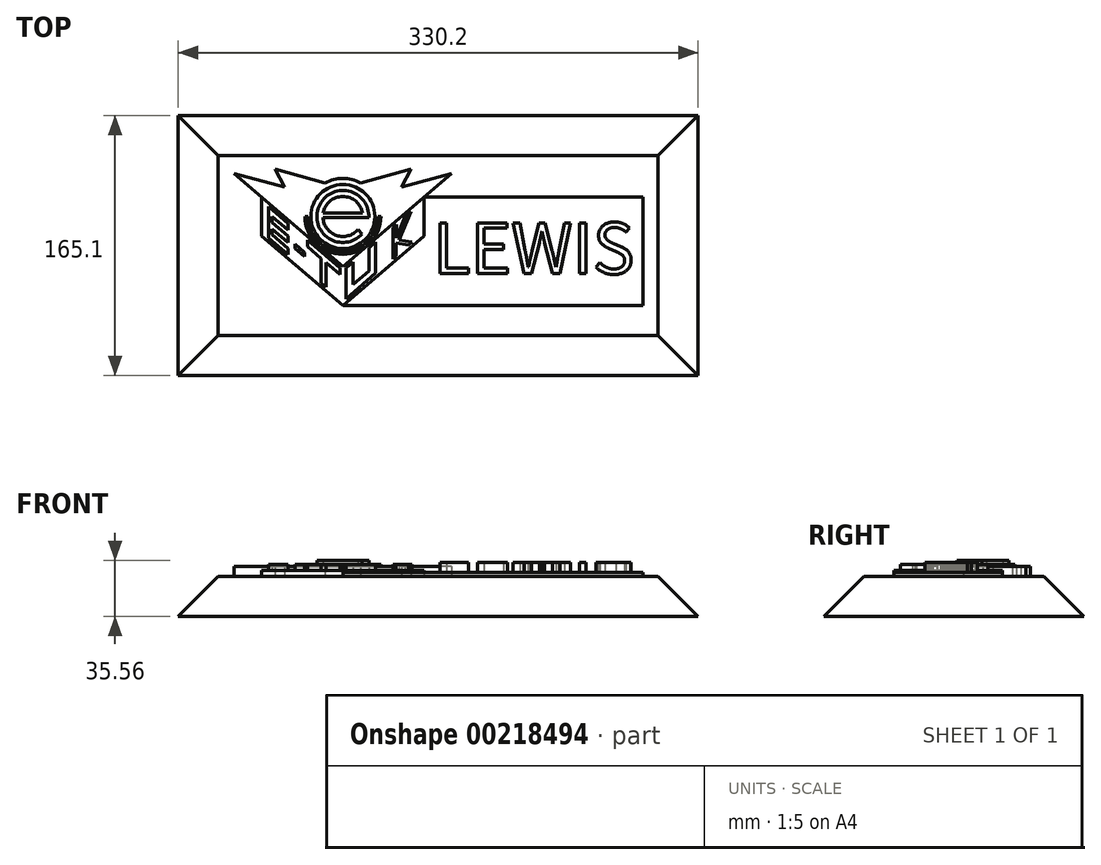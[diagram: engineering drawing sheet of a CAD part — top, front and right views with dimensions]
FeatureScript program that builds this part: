
annotation { "Feature Type Name" : "Feature", "Feature Type Description" : "" }
export const myFeature = defineFeature(function(context is Context, id is Id, definition is map)
    precondition{}
    {
        {
            var Q0;
            Q0=qCreatedBy(makeId("Top.planeOp"),FACE);
            var sketch = newSketch(context, id + "F0", { "sketchPlane" : qUnion([Q0])});
            skArc(sketch, "E0", {"start": v(12.53, 2.07) * mm, "mid": v(0, 12.7) * mm, "end": v(-12.53, 2.07) * mm});
            skArc(sketch, "E1", {"start": v(16.5, -0.78) * mm, "mid": v(-15.23, 6.37) * mm, "end": v(12.14, -11.18) * mm});
            skLineSegment(sketch, "E2", {"start": v(12.7, -0.78) * mm, "end": v(-12.68, -0.78) * mm});
            skLineSegment(sketch, "E3", {"start": v(-12.68, -0.78) * mm, "end": v(16.5, -0.78) * mm});
            skLineSegment(sketch, "E4", {"start": v(9.59, -8.33) * mm, "end": v(12.14, -11.18) * mm});
            skArc(sketch, "E5.trimOffspring", {"start": v(-12.68, -0.78) * mm, "mid": v(-4.08, -12.03) * mm, "end": v(9.59, -8.33) * mm});
            skLineSegment(sketch, "E6", {"start": v(-12.53, 2.07) * mm, "end": v(12.53, 2.07) * mm});
            skSolve(sketch);
        }
        {
            var Q0;
            Q0=makeQuery(id+"F0.imprint","IMPRINT",FACE,{"disambiguationData":[TD([[makeQuery(id+"F0.imprint","IMPRINT",EDGE,{"derivedFrom":sQuery(id+"F0.wireOp",EDGE,"E0")}),-1.0]])]});
            extrude(context, id + "F1", {"entities" : qUnion([Q0]), "depth" : 10.16 * mm});
        }
        {
            var Q0;
            Q0=qCreatedBy(makeId("Top.planeOp"),FACE);
            var sketch = newSketch(context, id + "F2", { "sketchPlane" : qUnion([Q0])});
            skCircle(sketch, "E7", {"center": v(0, 0) * mm, "radius": 20.32 * mm});
            skSolve(sketch);
        }
        {
            var Q0;
            Q0=qSketchRegion(id+"F2",true);
            extrude(context, id + "F3", {"entities" : qUnion([Q0]), "operationType" : NewBodyOperationType.ADD, "depth" : 7.62 * mm});
        }
        {
            var Q0;
            Q0=qCreatedBy(makeId("Top.planeOp"),FACE);
            var sketch = newSketch(context, id + "F4", { "sketchPlane" : qUnion([Q0])});
            skLineSegment(sketch, "E8", {"start": v(-69.02, 27.27) * mm, "end": v(-37.13, 18.72) * mm});
            skLineSegment(sketch, "E9", {"start": v(-37.13, 18.72) * mm, "end": v(-43.14, 30.14) * mm});
            skLineSegment(sketch, "E10", {"start": v(-43.14, 30.14) * mm, "end": v(-11.32, 21.31) * mm});
            skLineSegment(sketch, "E11", {"start": v(-69.02, 27.27) * mm, "end": v(0, -31.75) * mm});
            skLineSegment(sketch, "E12.MirrorCS", {"start": v(43.14, 30.14) * mm, "end": v(11.32, 21.31) * mm});
            skLineSegment(sketch, "E13.MirrorCS", {"start": v(69.02, 27.27) * mm, "end": v(0, -31.75) * mm});
            skLineSegment(sketch, "E14.MirrorCS", {"start": v(69.02, 27.27) * mm, "end": v(37.13, 18.72) * mm});
            skLineSegment(sketch, "E15.MirrorCS", {"start": v(37.13, 18.72) * mm, "end": v(43.14, 30.14) * mm});
            skArc(sketch, "E16.trimOffspring", {"start": v(11.32, 21.31) * mm, "mid": v(0, 24.13) * mm, "end": v(-11.32, 21.31) * mm});
            skSolve(sketch);
        }
        {
            var Q0;
            Q0=qSketchRegion(id+"F4",true);
            var Q1;
            Q1=makeQuery(id+"F2.imprint","IMPRINT",FACE,{"disambiguationData":[TD([[makeQuery(id+"F2.imprint","IMPRINT",EDGE,{"derivedFrom":sQuery(id+"F2.wireOp",EDGE,"E7")}),1.0]])]});
            extrude(context, id + "F5", {"entities" : qUnion([Q0, Q1]), "operationType" : NewBodyOperationType.ADD, "depth" : 6.35 * mm});
        }
        {
            var Q0;
            Q0=qCreatedBy(makeId("Top.planeOp"),FACE);
            var sketch = newSketch(context, id + "F6", { "sketchPlane" : qUnion([Q0])});
            skLineSegment(sketch, "E17", {"start": v(-51.6, -12.38) * mm, "end": v(0, -56.51) * mm});
            skLineSegment(sketch, "E18", {"start": v(0, -56.51) * mm, "end": v(51.6, -12.38) * mm});
            skLineSegment(sketch, "E19", {"start": v(-51.6, 12.38) * mm, "end": v(-51.6, -12.38) * mm});
            skLineSegment(sketch, "E20", {"start": v(51.6, 12.38) * mm, "end": v(51.6, -12.38) * mm});
            skLineSegment(sketch, "E21", {"start": v(-51.6, 12.38) * mm, "end": v(0, -31.75) * mm});
            skLineSegment(sketch, "E22", {"start": v(0, -31.75) * mm, "end": v(51.6, 12.38) * mm});
            skSolve(sketch);
        }
        {
            var Q0;
            Q0=qSketchRegion(id+"F6",true);
            extrude(context, id + "F7", {"entities" : qUnion([Q0]), "operationType" : NewBodyOperationType.ADD, "depth" : 3.8 * mm});
        }
        {
            var Q0;
            Q0=makeQuery(id+"F7.opExtrude","CAP_FACE",FACE,{"disambiguationData":[OSD([sQuery(id+"F6.wireOp",EDGE,"E17"),sQuery(id+"F6.wireOp",EDGE,"E18"),sQuery(id+"F6.wireOp",EDGE,"E19"),sQuery(id+"F6.wireOp",EDGE,"E20"),sQuery(id+"F6.wireOp",EDGE,"E21"),sQuery(id+"F6.wireOp",EDGE,"E22")])],"isStart":false});
            var sketch = newSketch(context, id + "F8", { "sketchPlane" : qUnion([Q0])});
            skPoint(sketch, "E23.startSnap0", {"position": v(-51.6, 0) * mm});
            skLineSegment(sketch, "E24", {"start": v(-51.6, -9.87) * mm, "end": v(-51.6, 9.87) * mm, "construction": true});
            skLineSegment(sketch, "E25", {"start": v(-47.26, 6.16) * mm, "end": v(-34.74, -4.55) * mm});
            skLineSegment(sketch, "E26", {"start": v(-34.74, -4.55) * mm, "end": v(-34.74, -8.63) * mm});
            skLineSegment(sketch, "E27", {"start": v(-34.74, -8.63) * mm, "end": v(-44.83, 0) * mm});
            skLineSegment(sketch, "E28", {"start": v(-44.83, 0) * mm, "end": v(-44.83, -3.75) * mm});
            skLineSegment(sketch, "E29", {"start": v(-44.83, -3.75) * mm, "end": v(-34.74, -12.38) * mm});
            skLineSegment(sketch, "E30", {"start": v(-34.74, -12.38) * mm, "end": v(-34.74, -16.46) * mm});
            skLineSegment(sketch, "E31", {"start": v(-34.74, -16.46) * mm, "end": v(-44.83, -7.83) * mm});
            skLineSegment(sketch, "E32", {"start": v(-44.83, -7.83) * mm, "end": v(-44.83, -11.58) * mm});
            skLineSegment(sketch, "E33", {"start": v(-44.83, -11.58) * mm, "end": v(-34.74, -20.21) * mm});
            skLineSegment(sketch, "E34", {"start": v(-34.74, -20.21) * mm, "end": v(-34.74, -24.3) * mm});
            skLineSegment(sketch, "E35", {"start": v(-34.74, -24.3) * mm, "end": v(-47.26, -13.59) * mm});
            skLineSegment(sketch, "E36", {"start": v(-47.26, 6.16) * mm, "end": v(-47.26, -13.59) * mm});
            skLineSegment(sketch, "E37", {"start": v(-30.38, -20.21) * mm, "end": v(-30.38, -17.65) * mm});
            skLineSegment(sketch, "E38", {"start": v(-30.38, -17.65) * mm, "end": v(-24.17, -22.96) * mm});
            skLineSegment(sketch, "E39", {"start": v(-24.17, -22.96) * mm, "end": v(-24.17, -25.53) * mm});
            skLineSegment(sketch, "E40", {"start": v(-24.17, -25.53) * mm, "end": v(-30.38, -20.21) * mm});
            skLineSegment(sketch, "E41", {"start": v(-22.38, -15.12) * mm, "end": v(-1.9, -32.63) * mm});
            skLineSegment(sketch, "E42", {"start": v(-1.9, -32.63) * mm, "end": v(-1.9, -36.71) * mm});
            skLineSegment(sketch, "E43", {"start": v(-1.9, -36.71) * mm, "end": v(-10.6, -29.28) * mm});
            skLineSegment(sketch, "E44", {"start": v(-10.6, -29.28) * mm, "end": v(-10.6, -44.95) * mm});
            skLineSegment(sketch, "E45", {"start": v(-10.6, -44.95) * mm, "end": v(-13.7, -42.3) * mm});
            skLineSegment(sketch, "E46", {"start": v(-13.7, -42.3) * mm, "end": v(-13.7, -26.63) * mm});
            skLineSegment(sketch, "E47", {"start": v(-13.7, -26.63) * mm, "end": v(-22.38, -19.2) * mm});
            skLineSegment(sketch, "E48", {"start": v(-22.38, -19.2) * mm, "end": v(-22.38, -15.12) * mm});
            skLineSegment(sketch, "E49", {"start": v(1.9, -32.62) * mm, "end": v(6.3, -28.86) * mm});
            skLineSegment(sketch, "E50", {"start": v(6.3, -28.86) * mm, "end": v(6.3, -43.26) * mm});
            skLineSegment(sketch, "E51", {"start": v(6.3, -43.26) * mm, "end": v(16.5, -34.54) * mm});
            skLineSegment(sketch, "E52", {"start": v(16.5, -34.54) * mm, "end": v(16.5, -20.14) * mm});
            skLineSegment(sketch, "E53", {"start": v(16.5, -20.14) * mm, "end": v(20.85, -16.3) * mm});
            skLineSegment(sketch, "E54", {"start": v(20.85, -16.3) * mm, "end": v(20.85, -36.06) * mm});
            skLineSegment(sketch, "E55", {"start": v(20.85, -36.06) * mm, "end": v(1.9, -52.37) * mm});
            skLineSegment(sketch, "E56", {"start": v(1.9, -52.37) * mm, "end": v(1.9, -32.62) * mm});
            skLineSegment(sketch, "E57", {"start": v(31.73, -7.12) * mm, "end": v(31.73, -27.15) * mm});
            skLineSegment(sketch, "E58", {"start": v(31.73, -27.15) * mm, "end": v(33.91, -25.22) * mm});
            skLineSegment(sketch, "E59", {"start": v(33.91, -25.22) * mm, "end": v(33.91, -16.82) * mm});
            skLineSegment(sketch, "E60", {"start": v(33.94, -13.64) * mm, "end": v(33.94, -5.23) * mm});
            skLineSegment(sketch, "E61", {"start": v(33.94, -5.23) * mm, "end": v(31.73, -7.12) * mm});
            skLineSegment(sketch, "E62", {"start": v(41.79, -18.27) * mm, "end": v(44, -16.38) * mm});
            skLineSegment(sketch, "E63", {"start": v(33.94, -13.64) * mm, "end": v(39.5, 0) * mm});
            skLineSegment(sketch, "E64", {"start": v(33.91, -16.82) * mm, "end": v(41.79, -18.27) * mm});
            skLineSegment(sketch, "E65", {"start": v(44, -16.38) * mm, "end": v(35.85, -14.87) * mm});
            skLineSegment(sketch, "E66", {"start": v(35.85, -14.87) * mm, "end": v(43.2, 3.16) * mm});
            skLineSegment(sketch, "E67", {"start": v(39.5, 0) * mm, "end": v(43.2, 3.16) * mm});
            skSolve(sketch);
        }
        {
            var Q0;
            Q0=qSketchRegion(id+"F8",true);
            extrude(context, id + "F9", {"entities" : qUnion([Q0]), "operationType" : NewBodyOperationType.ADD, "depth" : 3.8 * mm});
        }
        {
            var Q0;
            Q0=makeQuery(id+"F5.boolean.opBoolean","MERGE",FACE,{"derivedFrom":[makeQuery(id+"F5.opExtrude","CAP_FACE",FACE,{"disambiguationData":[OSD([sQuery(id+"F2.wireOp",EDGE,"E7")])],"isStart":false}),makeQuery(id+"F5.opExtrude","CAP_FACE",FACE,{"disambiguationData":[OSD([sQuery(id+"F4.wireOp",EDGE,"E8"),sQuery(id+"F4.wireOp",EDGE,"E9"),sQuery(id+"F4.wireOp",EDGE,"E10"),sQuery(id+"F4.wireOp",EDGE,"E11"),sQuery(id+"F4.wireOp",EDGE,"E13.MirrorCS"),sQuery(id+"F4.wireOp",EDGE,"E14.MirrorCS"),sQuery(id+"F4.wireOp",EDGE,"E12.MirrorCS"),sQuery(id+"F4.wireOp",EDGE,"E15.MirrorCS"),sQuery(id+"F4.wireOp",EDGE,"E16.trimOffspring")])],"isStart":false})]});
            var sketch = newSketch(context, id + "F10", { "sketchPlane" : qUnion([Q0])});
            skArc(sketch, "E68", {"start": v(-24.13, 0) * mm, "mid": v(0, -24.13) * mm, "end": v(24.13, 0) * mm});
            skArc(sketch, "E69", {"start": v(-22.23, 0) * mm, "mid": v(0, -22.23) * mm, "end": v(22.23, 0) * mm});
            skLineSegment(sketch, "E70", {"start": v(-24.13, 0) * mm, "end": v(-22.23, 0) * mm});
            skLineSegment(sketch, "E71", {"start": v(24.13, 0) * mm, "end": v(22.23, 0) * mm});
            skSolve(sketch);
        }
        {
            var Q0;
            Q0=qSketchRegion(id+"F10",true);
            extrude(context, id + "F11", {"entities" : qUnion([Q0]), "operationType" : NewBodyOperationType.ADD, "depth" : 1.27 * mm});
        }
        {
            var Q0;
            {var subQ0=sQuery(id+"F2.wireOp",EDGE,"E7");Q0=makeQuery(id+"F7.boolean.opBoolean","MERGE",FACE,{"derivedFrom":[makeQuery(id+"F5.boolean.opBoolean","MERGE",FACE,{"derivedFrom":[makeQuery(id+"F3.boolean.opBoolean","MERGE",FACE,{"derivedFrom":[makeQuery(id+"F1.opExtrude","CAP_FACE",FACE,{"disambiguationData":[OSD([sQuery(id+"F0.wireOp",EDGE,"E0"),sQuery(id+"F0.wireOp",EDGE,"E1"),sQuery(id+"F0.wireOp",EDGE,"E3"),sQuery(id+"F0.wireOp",EDGE,"E4"),sQuery(id+"F0.wireOp",EDGE,"E5.trimOffspring"),sQuery(id+"F0.wireOp",EDGE,"E6")])],"isStart":true}),makeQuery(id+"F3.opExtrude","CAP_FACE",FACE,{"disambiguationData":[OSD([subQ0])],"isStart":true})]}),makeQuery(id+"F5.opExtrude","CAP_FACE",FACE,{"disambiguationData":[OSD([subQ0])],"isStart":true}),makeQuery(id+"F5.opExtrude","CAP_FACE",FACE,{"disambiguationData":[OSD([sQuery(id+"F4.wireOp",EDGE,"E8"),sQuery(id+"F4.wireOp",EDGE,"E9"),sQuery(id+"F4.wireOp",EDGE,"E10"),sQuery(id+"F4.wireOp",EDGE,"E11"),sQuery(id+"F4.wireOp",EDGE,"E13.MirrorCS"),sQuery(id+"F4.wireOp",EDGE,"E14.MirrorCS"),sQuery(id+"F4.wireOp",EDGE,"E12.MirrorCS"),sQuery(id+"F4.wireOp",EDGE,"E15.MirrorCS"),sQuery(id+"F4.wireOp",EDGE,"E16.trimOffspring")])],"isStart":true})]}),makeQuery(id+"F7.opExtrude","CAP_FACE",FACE,{"disambiguationData":[OSD([sQuery(id+"F6.wireOp",EDGE,"E17"),sQuery(id+"F6.wireOp",EDGE,"E18"),sQuery(id+"F6.wireOp",EDGE,"E19"),sQuery(id+"F6.wireOp",EDGE,"E20"),sQuery(id+"F6.wireOp",EDGE,"E21"),sQuery(id+"F6.wireOp",EDGE,"E22")])],"isStart":true})]});}
            var sketch = newSketch(context, id + "F12", { "sketchPlane" : qUnion([Q0])});
            skLineSegment(sketch, "E72.bottom", {"start": v(0, 56.51) * mm, "end": v(190.5, 56.51) * mm});
            skLineSegment(sketch, "E72.right", {"start": v(190.5, 56.51) * mm, "end": v(190.5, -12.38) * mm});
            skLineSegment(sketch, "E73", {"start": v(51.6, -12.38) * mm, "end": v(190.5, -12.38) * mm});
            skLineSegment(sketch, "E74", {"start": v(0, 56.51) * mm, "end": v(51.6, 12.38) * mm});
            skLineSegment(sketch, "E75", {"start": v(51.6, 12.38) * mm, "end": v(51.6, -12.38) * mm});
            skSolve(sketch);
        }
        {
            var Q0;
            Q0=qSketchRegion(id+"F12",true);
            extrude(context, id + "F13", {"entities" : qUnion([Q0]), "operationType" : NewBodyOperationType.ADD, "oppositeDirection" : true, "depth" : 2.54 * mm});
        }
        {
            var Q0;
            Q0=makeQuery(id+"F13.opExtrude","CAP_FACE",FACE,{"disambiguationData":[OSD([sQuery(id+"F12.wireOp",EDGE,"E72.bottom"),sQuery(id+"F12.wireOp",EDGE,"E72.right"),sQuery(id+"F12.wireOp",EDGE,"E73"),sQuery(id+"F12.wireOp",EDGE,"E74"),sQuery(id+"F12.wireOp",EDGE,"E75")])],"isStart":false});
            var sketch = newSketch(context, id + "F14", { "sketchPlane" : qUnion([Q0])});
            skLineSegment(sketch, "E76", {"start": v(51.6, 12.38) * mm, "end": v(51.6, -56.51) * mm, "construction": true});
            skLineSegment(sketch, "E77", {"start": v(51.6, -56.51) * mm, "end": v(190.5, -56.51) * mm, "construction": true});
            skLineSegment(sketch, "E78", {"start": v(190.5, -56.51) * mm, "end": v(190.5, 12.38) * mm, "construction": true});
            skLineSegment(sketch, "E79", {"start": v(190.5, 12.38) * mm, "end": v(51.6, 12.38) * mm, "construction": true});
            skPoint(sketch, "E80.startSnap0", {"position": v(51.6, 0) * mm});
            skPoint(sketch, "E80.endSnap0", {"position": v(51.6, 0) * mm});
            skLineSegment(sketch, "E81", {"start": v(185.58, -36.36) * mm, "end": v(57.26, -36.36) * mm, "construction": true});
            skLineSegment(sketch, "E82", {"start": v(178.12, -4.6) * mm, "end": v(57.26, -4.6) * mm, "construction": true});
            skText(sketch, "E83", { "text": "LEWIS", "fontName": "NotoSansCJKkr-Regular.otf"});
            const initialGuessF14  = {"E83": [0.05726, -0.03636, 1, 0, 0.03175]};
            skSetInitialGuess(sketch, initialGuessF14);
            skSolve(sketch);
        }
        {
            var Q0;
            Q0=qSketchRegion(id+"F14",true);
            extrude(context, id + "F15", {"entities" : qUnion([Q0]), "operationType" : NewBodyOperationType.ADD, "depth" : 6.35 * mm});
        }
        {
            var Q0;
            Q0=makeQuery(id+"F13.opExtrude","CAP_FACE",FACE,{"disambiguationData":[OSD([sQuery(id+"F12.wireOp",EDGE,"E72.bottom"),sQuery(id+"F12.wireOp",EDGE,"E72.right"),sQuery(id+"F12.wireOp",EDGE,"E73"),sQuery(id+"F12.wireOp",EDGE,"E74"),sQuery(id+"F12.wireOp",EDGE,"E75")])],"isStart":true});
            var sketch = newSketch(context, id + "F16", { "sketchPlane" : qUnion([Q0])});
            skLineSegment(sketch, "E84.bottom", {"start": v(-79.18, -38.74) * mm, "end": v(200.22, -38.74) * mm});
            skLineSegment(sketch, "E84.top", {"start": v(-79.18, 75.56) * mm, "end": v(200.22, 75.56) * mm});
            skLineSegment(sketch, "E84.left", {"start": v(-79.18, -38.74) * mm, "end": v(-79.18, 75.56) * mm});
            skLineSegment(sketch, "E84.right", {"start": v(200.22, -38.74) * mm, "end": v(200.22, 75.56) * mm});
            skSolve(sketch);
        }
        {
            var Q0;
            Q0=qSketchRegion(id+"F16",true);
            extrude(context, id + "F17", {"entities" : qUnion([Q0]), "operationType" : NewBodyOperationType.ADD, "depth" : 25.4 * mm, "hasDraft" : true, "draftAngle" : 45 * degree});
        }
    });
